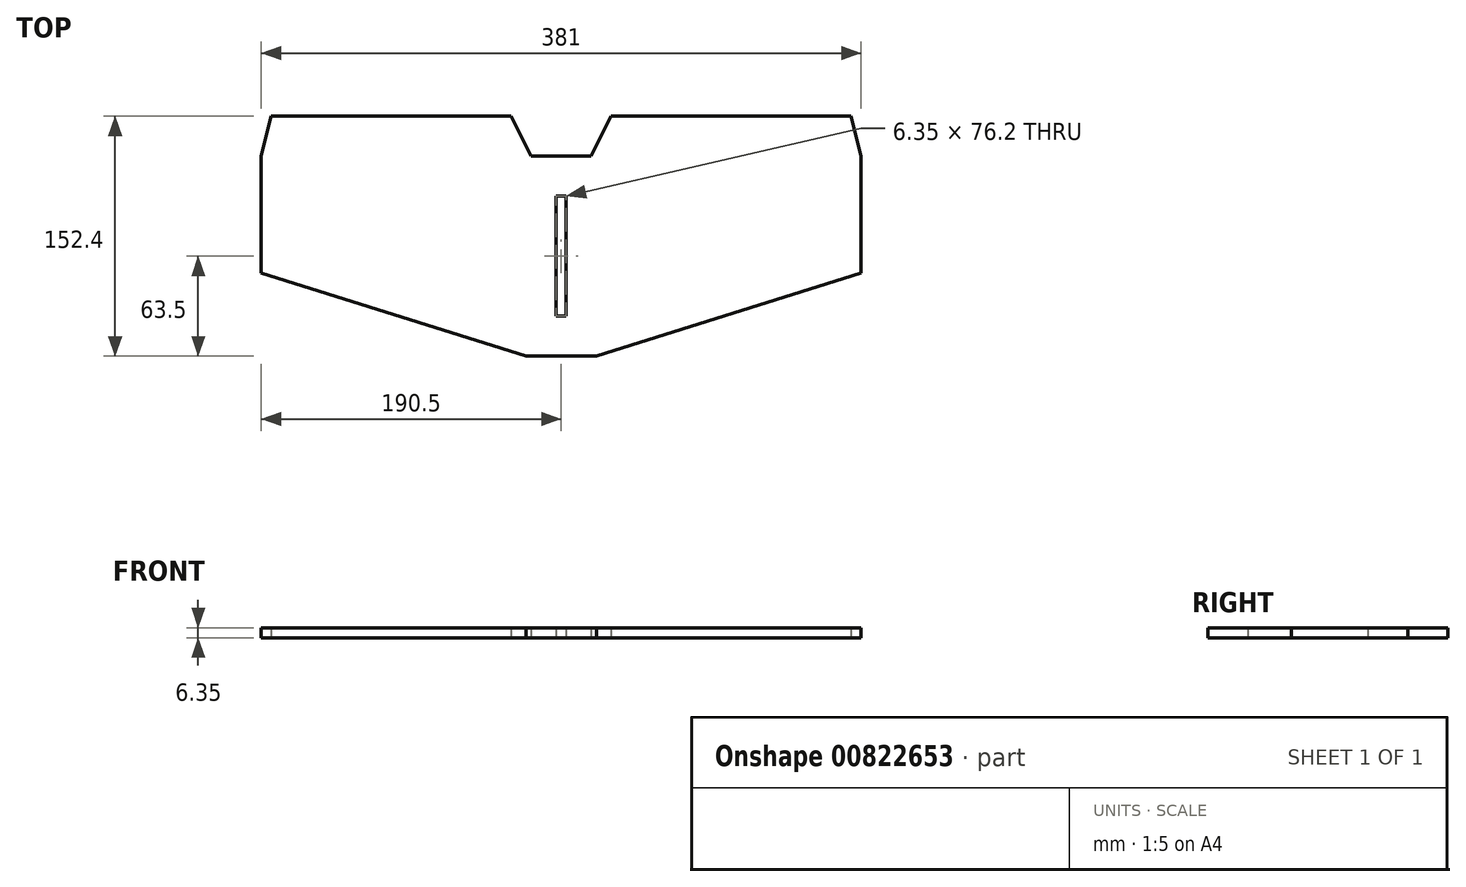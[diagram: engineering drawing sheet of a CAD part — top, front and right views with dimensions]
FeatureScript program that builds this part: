
annotation { "Feature Type Name" : "Feature", "Feature Type Description" : "" }
export const myFeature = defineFeature(function(context is Context, id is Id, definition is map)
    precondition{}
    {
        {
            var Q0;
            Q0=qCreatedBy(makeId("Top.planeOp"),FACE);
            var sketch = newSketch(context, id + "F0", { "sketchPlane" : qUnion([Q0])});
            skLineSegment(sketch, "E0", {"start": v(-190.5, -10.6) * mm, "end": v(-190.5, 63.5) * mm});
            skLineSegment(sketch, "E1", {"start": v(-190.5, 63.5) * mm, "end": v(0, 63.5) * mm});
            skLineSegment(sketch, "E2", {"start": v(-31.75, 88.9) * mm, "end": v(-184.15, 88.9) * mm});
            skLineSegment(sketch, "E3", {"start": v(-184.15, 88.9) * mm, "end": v(-190.5, 63.5) * mm});
            skLineSegment(sketch, "E4.MirrorCS", {"start": v(31.75, 88.9) * mm, "end": v(184.15, 88.9) * mm});
            skLineSegment(sketch, "E5.MirrorCS", {"start": v(190.5, 63.5) * mm, "end": v(0, 63.5) * mm});
            skLineSegment(sketch, "E6.MirrorCS", {"start": v(184.15, 88.9) * mm, "end": v(190.5, 63.5) * mm});
            skLineSegment(sketch, "E7.MirrorCS", {"start": v(190.5, -10.6) * mm, "end": v(190.5, 63.5) * mm});
            skLineSegment(sketch, "E8", {"start": v(-31.75, 88.9) * mm, "end": v(-19.05, 63.5) * mm});
            skLineSegment(sketch, "E9.MirrorCS", {"start": v(31.75, 88.9) * mm, "end": v(19.05, 63.5) * mm});
            skLineSegment(sketch, "E10", {"start": v(0, -63.5) * mm, "end": v(-22.25, -63.5) * mm});
            skLineSegment(sketch, "E11", {"start": v(-190.5, -10.6) * mm, "end": v(-22.25, -63.5) * mm});
            skLineSegment(sketch, "E12.MirrorCS", {"start": v(0, -63.5) * mm, "end": v(22.25, -63.5) * mm});
            skLineSegment(sketch, "E13.MirrorCS", {"start": v(190.5, -10.6) * mm, "end": v(22.25, -63.5) * mm});
            skLineSegment(sketch, "E14", {"start": v(0, -38.1) * mm, "end": v(-3.17, -38.1) * mm});
            skLineSegment(sketch, "E15", {"start": v(-3.17, -38.1) * mm, "end": v(-3.18, 38.1) * mm});
            skLineSegment(sketch, "E16", {"start": v(-3.17, 38.1) * mm, "end": v(0, 38.1) * mm});
            skLineSegment(sketch, "E17.MirrorCS", {"start": v(3.17, 38.1) * mm, "end": v(0, 38.1) * mm});
            skLineSegment(sketch, "E18.MirrorCS", {"start": v(3.18, -38.1) * mm, "end": v(3.17, 38.1) * mm});
            skLineSegment(sketch, "E19.MirrorCS", {"start": v(0, -38.1) * mm, "end": v(3.17, -38.1) * mm});
            skSolve(sketch);
        }
        {
            var Q0;
            Q0 = qSketchRegion(id + "F0", true);
            extrude(context, id + "F1", {"entities" : qUnion([Q0]), "depth" : 6.35 * mm, "offsetDistance" : 25.4 * mm});
        }
    });
